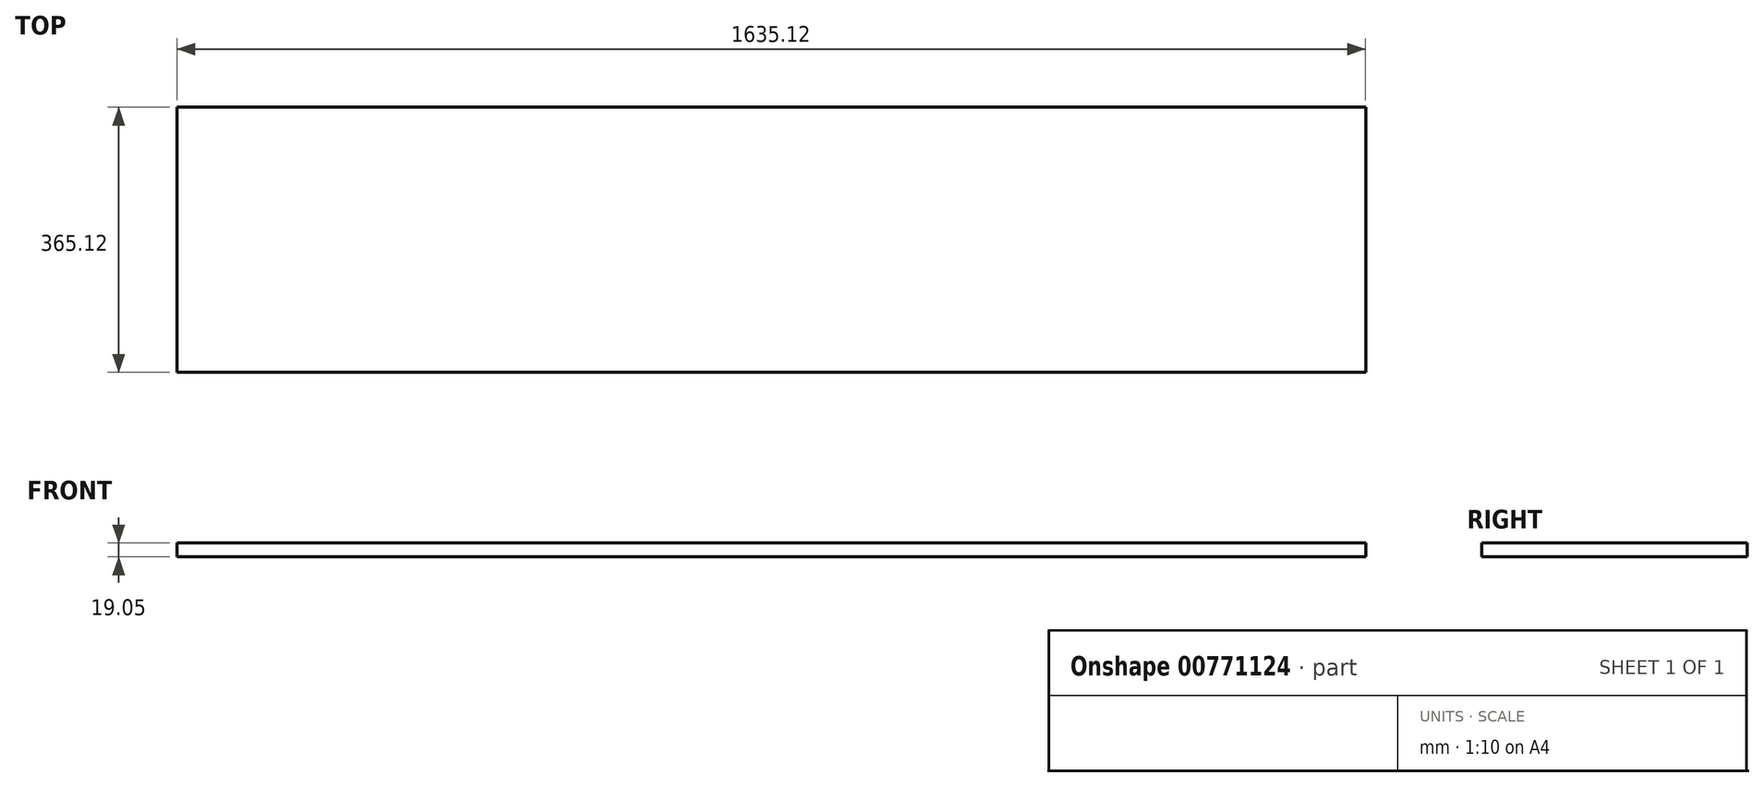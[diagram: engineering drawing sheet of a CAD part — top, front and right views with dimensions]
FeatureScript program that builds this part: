
annotation { "Feature Type Name" : "Feature", "Feature Type Description" : "" }
export const myFeature = defineFeature(function(context is Context, id is Id, definition is map)
    precondition{}
    {
        {
            var Q0;
            Q0=qCreatedBy(makeId("Top.planeOp"),FACE);
            var sketch = newSketch(context, id + "F0", { "sketchPlane" : qUnion([Q0])});
            skLineSegment(sketch, "E0.bottom", {"start": v(-817.56, 182.56) * mm, "end": v(817.56, 182.56) * mm});
            skLineSegment(sketch, "E0.top", {"start": v(-817.56, -182.56) * mm, "end": v(817.56, -182.56) * mm});
            skLineSegment(sketch, "E0.left", {"start": v(-817.56, 182.56) * mm, "end": v(-817.56, -182.56) * mm});
            skLineSegment(sketch, "E0.right", {"start": v(817.56, 182.56) * mm, "end": v(817.56, -182.56) * mm});
            skPoint(sketch, "E0.middle", {"position": v(0, 0) * mm});
            skSolve(sketch);
        }
        {
            var Q0;
            Q0 = qSketchRegion(id + "F0", true);
            extrude(context, id + "F1", {"entities" : qUnion([Q0]), "depth" : 19.05 * mm, "offsetDistance" : 25.4 * mm});
        }
    });
